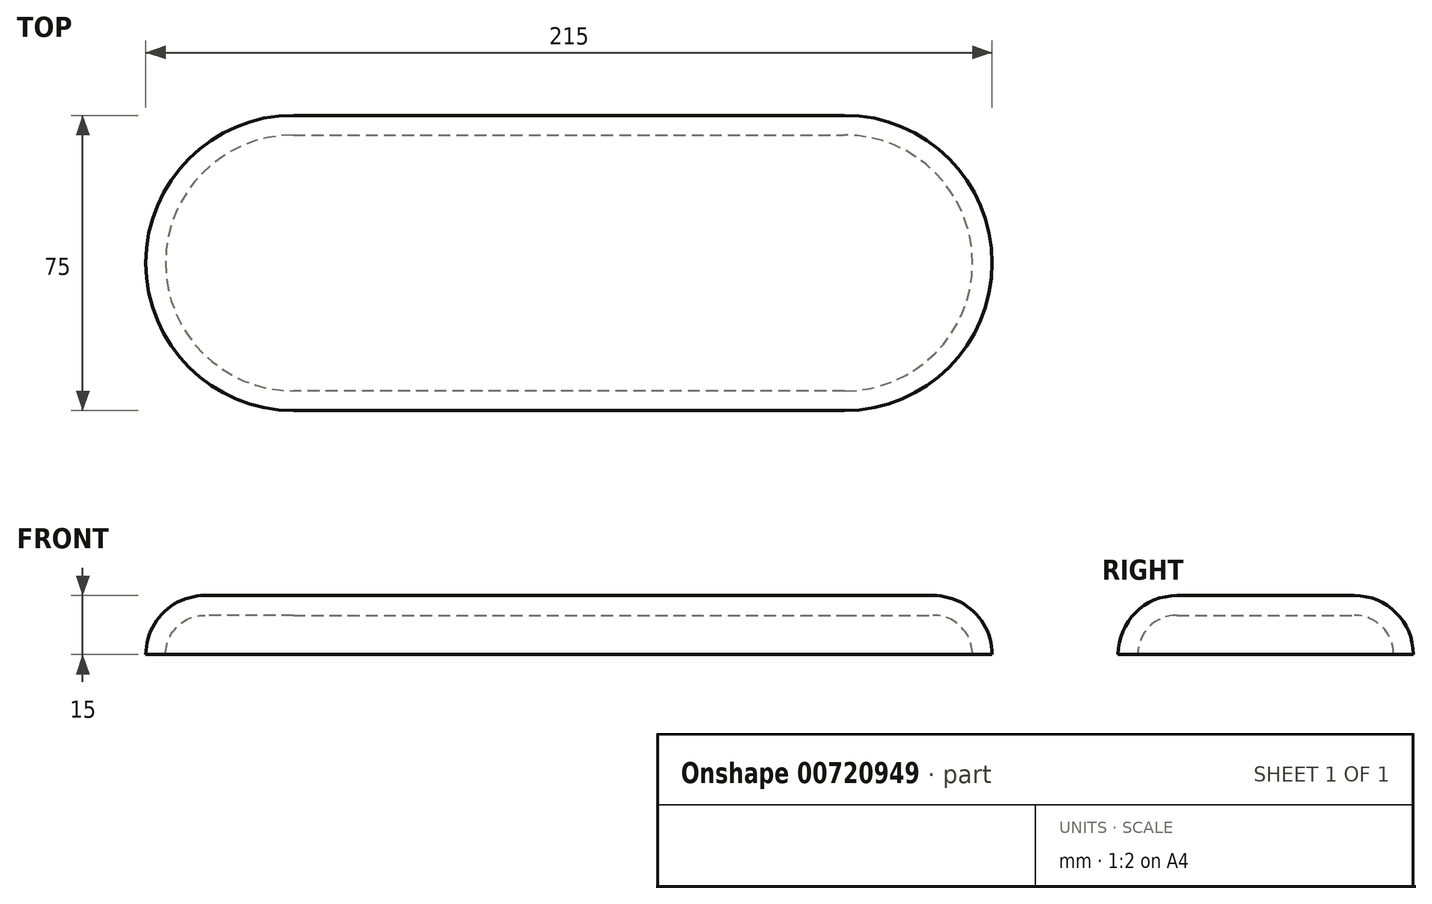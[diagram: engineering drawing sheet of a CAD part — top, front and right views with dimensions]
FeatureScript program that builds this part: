
annotation { "Feature Type Name" : "Feature", "Feature Type Description" : "" }
export const myFeature = defineFeature(function(context is Context, id is Id, definition is map)
    precondition{}
    {
        {
            var Q0;
            Q0=qCreatedBy(makeId("Top.planeOp"),FACE);
            var sketch = newSketch(context, id + "F0", { "sketchPlane" : qUnion([Q0])});
            skLineSegment(sketch, "E0", {"start": v(-71.08, 0) * mm, "end": v(68.92, 0) * mm});
            skLineSegment(sketch, "E1.left", {"start": v(-71.08, 0) * mm, "end": v(-71.08, 0) * mm});
            skLineSegment(sketch, "E1.right", {"start": v(68.92, 0) * mm, "end": v(68.92, 0) * mm});
            skLineSegment(sketch, "E2.top", {"start": v(-71.08, -75) * mm, "end": v(68.92, -75) * mm});
            skLineSegment(sketch, "E2.left", {"start": v(-71.08, 0) * mm, "end": v(-71.08, -75) * mm});
            skLineSegment(sketch, "E2.right", {"start": v(68.92, 0) * mm, "end": v(68.92, -75) * mm});
            skArc(sketch, "E3", {"start": v(-71.08, 0) * mm, "mid": v(-108.58, -37.5) * mm, "end": v(-71.08, -75) * mm});
            skArc(sketch, "E4", {"start": v(68.92, -75) * mm, "mid": v(106.42, -37.5) * mm, "end": v(68.92, 0) * mm});
            skSolve(sketch);
        }
        {
            var Q0;
            Q0=makeQuery(id+"F0.imprint","IMPRINT",FACE,{"disambiguationData":[TD([[makeQuery(id+"F0.imprint","IMPRINT",EDGE,{"derivedFrom":sQuery(id+"F0.wireOp",EDGE,"E0")}),-1.0]])]});
            var Q1;
            Q1=makeQuery(id+"F0.imprint","IMPRINT",FACE,{"disambiguationData":[TD([[makeQuery(id+"F0.imprint","IMPRINT",EDGE,{"derivedFrom":sQuery(id+"F0.wireOp",EDGE,"E2.left")}),-1.0]])]});
            var Q2;
            Q2=makeQuery(id+"F0.imprint","IMPRINT",FACE,{"disambiguationData":[TD([[makeQuery(id+"F0.imprint","IMPRINT",EDGE,{"derivedFrom":sQuery(id+"F0.wireOp",EDGE,"E2.right")}),1.0]])]});
            extrude(context, id + "F1", {"entities" : qUnion([Q0, Q1, Q2]), "depth" : 15 * mm, "offsetDistance" : 25 * mm});
        }
        {
            var Q0;
            Q0=makeQuery(id+"F1.opExtrude","CAP_EDGE",EDGE,{"disambiguationData":[OSD([sQuery(id+"F0.wireOp",EDGE,"E3")])],"isStart":false});
            fillet(context, id + "F2", {"entities" : qUnion([Q0]), "radius" : 15 * mm, "tangentPropagation" : true, "allowEdgeOverflow" : false});
        }
        {
            var Q0;
            Q0=makeQuery(id+"F1.opExtrude","CAP_FACE",FACE,{"disambiguationData":[OSD([sQuery(id+"F0.wireOp",EDGE,"E0"),sQuery(id+"F0.wireOp",EDGE,"E2.top"),sQuery(id+"F0.wireOp",EDGE,"E3"),sQuery(id+"F0.wireOp",EDGE,"E4")])],"isStart":true});
            shell(context, id + "F3", {"entities" : qUnion([Q0]), "thickness" : 5 * mm});
        }
    });
